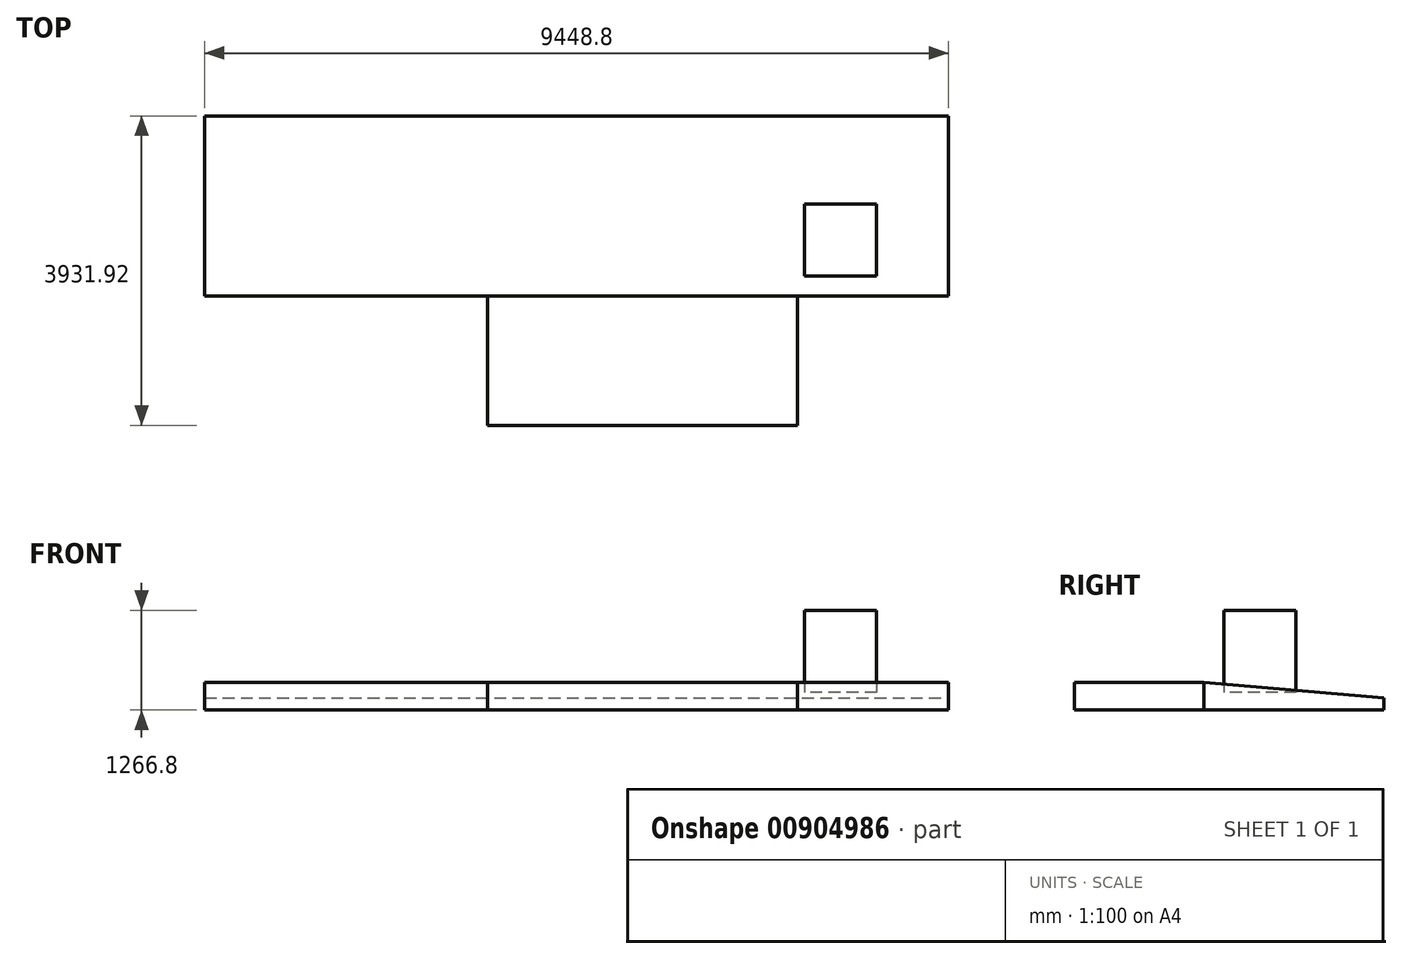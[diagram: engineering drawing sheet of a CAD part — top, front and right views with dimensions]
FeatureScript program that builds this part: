
annotation { "Feature Type Name" : "Feature", "Feature Type Description" : "" }
export const myFeature = defineFeature(function(context is Context, id is Id, definition is map)
    precondition{}
    {
        {
            var Q0;
            Q0=qCreatedBy(makeId("Right.planeOp"),FACE);
            var sketch = newSketch(context, id + "F0", { "sketchPlane" : qUnion([Q0])});
            skLineSegment(sketch, "E0", {"start": v(0, 0) * mm, "end": v(2286, -200) * mm});
            skLineSegment(sketch, "E1", {"start": v(0, -200) * mm, "end": v(0, 0) * mm});
            skLineSegment(sketch, "E2", {"start": v(0, -200) * mm, "end": v(0, -352.4) * mm});
            skLineSegment(sketch, "E3", {"start": v(0, -352.4) * mm, "end": v(2286, -352.4) * mm});
            skLineSegment(sketch, "E4", {"start": v(2286, -352.4) * mm, "end": v(2286, -200) * mm});
            skSolve(sketch);
        }
        {
            var Q0;
            Q0 = qSketchRegion(id + "F0", true);
            extrude(context, id + "F1", {"entities" : qUnion([Q0]), "oppositeDirection" : true, "depth" : 9448.8 * mm, "offsetDistance" : 25.4 * mm});
        }
        {
            var Q0;
            Q0=qCreatedBy(makeId("Top.planeOp"),FACE);
            var sketch = newSketch(context, id + "F2", { "sketchPlane" : qUnion([Q0])});
            skLineSegment(sketch, "E5", {"start": v(-5852.16, 0) * mm, "end": v(-5852.16, -1645.92) * mm});
            skLineSegment(sketch, "E6", {"start": v(-5852.16, -1645.92) * mm, "end": v(-1920.24, -1645.92) * mm});
            skLineSegment(sketch, "E7", {"start": v(-1920.24, -1645.92) * mm, "end": v(-1920.24, 0) * mm});
            skLineSegment(sketch, "E8", {"start": v(-1920.24, 0) * mm, "end": v(-5852.16, 0) * mm});
            skSolve(sketch);
        }
        {
            var Q0;
            Q0 = qSketchRegion(id + "F2", true);
            var Q1;
            Q1=makeQuery(id+"F1.opExtrude","SWEPT_FACE",FACE,{"disambiguationData":[OSD([sQuery(id+"F0.wireOp",EDGE,"E3")])]});
            extrude(context, id + "F3", {"entities" : qUnion([Q0]), "operationType" : NewBodyOperationType.ADD, "endBound" : BoundingType.UP_TO_SURFACE, "oppositeDirection" : true, "depth" : 25.4 * mm, "endBoundEntityFace" : qUnion([Q1]), "offsetDistance" : 25.4 * mm});
        }
        {
            var Q0;
            Q0=qCreatedBy(makeId("Top.planeOp"),FACE);
            var sketch = newSketch(context, id + "F4", { "sketchPlane" : qUnion([Q0])});
            skLineSegment(sketch, "E9.bottom", {"start": v(-914.4, 1168.4) * mm, "end": v(-1828.8, 1168.4) * mm});
            skLineSegment(sketch, "E9.top", {"start": v(-914.4, 254) * mm, "end": v(-1828.8, 254) * mm});
            skLineSegment(sketch, "E9.left", {"start": v(-914.4, 1168.4) * mm, "end": v(-914.4, 254) * mm});
            skLineSegment(sketch, "E9.right", {"start": v(-1828.8, 1168.4) * mm, "end": v(-1828.8, 254) * mm});
            skPoint(sketch, "E9.middle", {"position": v(-1371.6, 711.2) * mm});
            skSolve(sketch);
        }
        {
            var Q0;
            Q0 = qSketchRegion(id + "F4", true);
            extrude(context, id + "F5", {"entities" : qUnion([Q0]), "depth" : 914.4 * mm, "offsetDistance" : 25.4 * mm, "hasSecondDirection" : true, "secondDirectionOppositeDirection" : true, "secondDirectionDepth" : 127 * mm});
        }
    });
